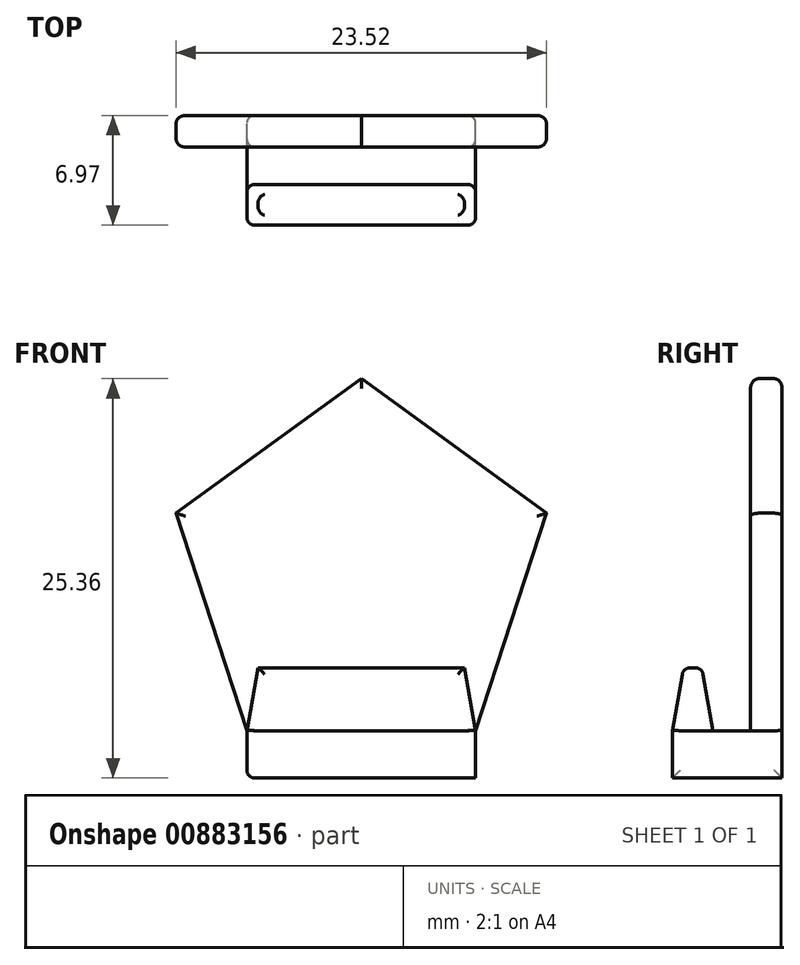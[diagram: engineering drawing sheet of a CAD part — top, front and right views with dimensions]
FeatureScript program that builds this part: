
annotation { "Feature Type Name" : "Feature", "Feature Type Description" : "" }
export const myFeature = defineFeature(function(context is Context, id is Id, definition is map)
    precondition{}
    {
        {
            var Q0;
            Q0=qCreatedBy(makeId("Front.planeOp"),FACE);
            var sketch = newSketch(context, id + "F0", { "sketchPlane" : qUnion([Q0])});
            skCircle(sketch, "E0.cCircle", {"center": v(0, 10) * mm, "radius": 10 * mm, "construction": true});
            skLineSegment(sketch, "E0.0", {"start": v(0, 22.36) * mm, "end": v(11.76, 13.82) * mm});
            skLineSegment(sketch, "E0.1", {"start": v(11.76, 13.82) * mm, "end": v(7.27, 0) * mm});
            skLineSegment(sketch, "E0.2", {"start": v(7.27, 0) * mm, "end": v(-7.27, 0) * mm});
            skLineSegment(sketch, "E0.3", {"start": v(-7.27, 0) * mm, "end": v(-11.76, 13.82) * mm});
            skLineSegment(sketch, "E0.4", {"start": v(-11.76, 13.82) * mm, "end": v(0, 22.36) * mm});
            skPoint(sketch, "E0.0.midPoint", {"position": v(5.88, 18.1) * mm});
            skSolve(sketch);
        }
        {
            var Q0;
            Q0=makeQuery(id+"F0.imprint","IMPRINT",FACE,{"disambiguationData":[TD([[makeQuery(id+"F0.imprint","IMPRINT",EDGE,{"derivedFrom":sQuery(id+"F0.wireOp",EDGE,"E0.0")}),-1.0]])]});
            extrude(context, id + "F1", {"entities" : qUnion([Q0]), "depth" : 2 * mm, "offsetDistance" : 25 * mm});
        }
        {
            var Q0;
            Q0=qCreatedBy(makeId("Top.planeOp"),FACE);
            var sketch = newSketch(context, id + "F2", { "sketchPlane" : qUnion([Q0])});
            skLineSegment(sketch, "E1.bottom", {"start": v(-7.27, -6.97) * mm, "end": v(7.27, -6.97) * mm});
            skLineSegment(sketch, "E1.top", {"start": v(-7.27, 0) * mm, "end": v(7.27, 0) * mm});
            skLineSegment(sketch, "E1.left", {"start": v(-7.27, -6.97) * mm, "end": v(-7.27, 0) * mm});
            skLineSegment(sketch, "E1.right", {"start": v(7.27, -6.97) * mm, "end": v(7.27, 0) * mm});
            skLineSegment(sketch, "E2", {"start": v(-7.27, -4.38) * mm, "end": v(7.27, -4.38) * mm});
            skSolve(sketch);
        }
        {
            var Q0;
            {var subQ0=sQuery(id+"F2.wireOp",EDGE,"E1.top");Q0=makeQuery(id+"F2.imprint","IMPRINT",FACE,{"disambiguationData":[TD([[makeQuery(id+"F2.imprint","IMPRINT",EDGE,{"derivedFrom":subQ0}),-1.0]])]});}
            var Q1;
            {var subQ0=sQuery(id+"F2.wireOp",EDGE,"E1.bottom");Q1=makeQuery(id+"F2.imprint","IMPRINT",FACE,{"disambiguationData":[TD([[makeQuery(id+"F2.imprint","IMPRINT",EDGE,{"derivedFrom":subQ0}),1.0]])]});}
            extrude(context, id + "F3", {"entities" : qUnion([Q0, Q1]), "operationType" : NewBodyOperationType.ADD, "oppositeDirection" : true, "depth" : 3 * mm, "offsetDistance" : 25 * mm});
        }
        {
            var Q0;
            {var subQ0=sQuery(id+"F2.wireOp",EDGE,"E1.bottom");Q0=makeQuery(id+"F2.imprint","IMPRINT",FACE,{"disambiguationData":[TD([[makeQuery(id+"F2.imprint","IMPRINT",EDGE,{"derivedFrom":subQ0}),1.0]])]});}
            extrude(context, id + "F4", {"entities" : qUnion([Q0]), "operationType" : NewBodyOperationType.ADD, "depth" : 4 * mm, "offsetDistance" : 25 * mm, "hasDraft" : true, "draftAngle" : 10 * degree, "draftPullDirection" : true});
        }
        {
            var Q0;
            Q0=makeQuery(id+"F4.opExtrude","SWEPT_EDGE",EDGE,{"disambiguationData":[OSD([sQuery(id+"F2.wireOp",EDGE,"E1.bottom"),sQuery(id+"F2.wireOp",EDGE,"E1.left")])]});
            var Q1;
            Q1=makeQuery(id+"F3.opExtrude","SWEPT_EDGE",EDGE,{"disambiguationData":[OSD([sQuery(id+"F2.wireOp",EDGE,"E1.bottom"),sQuery(id+"F2.wireOp",EDGE,"E1.left")])]});
            var Q2;
            Q2=makeQuery(id+"F4.opExtrude","CAP_EDGE",EDGE,{"disambiguationData":[OSD([sQuery(id+"F2.wireOp",EDGE,"E1.bottom")])],"isStart":false});
            var Q3;
            Q3=makeQuery(id+"F4.opExtrude","CAP_EDGE",EDGE,{"disambiguationData":[OSD([sQuery(id+"F2.wireOp",EDGE,"E2")])],"isStart":false});
            var Q4;
            Q4=makeQuery(id+"F3.opExtrude","CAP_EDGE",EDGE,{"disambiguationData":[OSD([sQuery(id+"F2.wireOp",EDGE,"E1.left")])],"isStart":false});
            var Q5;
            Q5=makeQuery(id+"F3.opExtrude","SWEPT_EDGE",EDGE,{"disambiguationData":[OSD([sQuery(id+"F2.wireOp",EDGE,"E1.bottom"),sQuery(id+"F2.wireOp",EDGE,"E1.right")])]});
            var Q6;
            Q6=makeQuery(id+"F4.opExtrude","SWEPT_EDGE",EDGE,{"disambiguationData":[OSD([sQuery(id+"F2.wireOp",EDGE,"E1.bottom"),sQuery(id+"F2.wireOp",EDGE,"E1.right")])]});
            var Q7;
            Q7=makeQuery(id+"F4.opExtrude","SWEPT_EDGE",EDGE,{"disambiguationData":[OSD([sQuery(id+"F2.wireOp",EDGE,"E1.right"),sQuery(id+"F2.wireOp",EDGE,"E2")])]});
            var Q8;
            Q8=makeQuery(id+"F4.opExtrude","SWEPT_EDGE",EDGE,{"disambiguationData":[OSD([sQuery(id+"F2.wireOp",EDGE,"E1.left"),sQuery(id+"F2.wireOp",EDGE,"E2")])]});
            var Q9;
            Q9=makeQuery(id+"F3.opExtrude","SWEPT_EDGE",EDGE,{"disambiguationData":[OSD([sQuery(id+"F2.wireOp",EDGE,"E1.top"),sQuery(id+"F2.wireOp",EDGE,"E1.left")])]});
            var Q10;
            Q10=makeQuery(id+"F1.opExtrude","CAP_EDGE",EDGE,{"disambiguationData":[OSD([sQuery(id+"F0.wireOp",EDGE,"E0.3")])],"isStart":true});
            var Q11;
            Q11=makeQuery(id+"F3.opExtrude","SWEPT_EDGE",EDGE,{"disambiguationData":[OSD([sQuery(id+"F2.wireOp",EDGE,"E1.top"),sQuery(id+"F2.wireOp",EDGE,"E1.right")])]});
            var Q12;
            Q12=makeQuery(id+"F1.opExtrude","CAP_EDGE",EDGE,{"disambiguationData":[OSD([sQuery(id+"F0.wireOp",EDGE,"E0.1")])],"isStart":true});
            var Q13;
            Q13=makeQuery(id+"F1.opExtrude","CAP_EDGE",EDGE,{"disambiguationData":[OSD([sQuery(id+"F0.wireOp",EDGE,"E0.0")])],"isStart":true});
            var Q14;
            Q14=makeQuery(id+"F1.opExtrude","CAP_EDGE",EDGE,{"disambiguationData":[OSD([sQuery(id+"F0.wireOp",EDGE,"E0.4")])],"isStart":true});
            var Q15;
            Q15=makeQuery(id+"F1.opExtrude","CAP_EDGE",EDGE,{"disambiguationData":[OSD([sQuery(id+"F0.wireOp",EDGE,"E0.0")])],"isStart":false});
            var Q16;
            Q16=makeQuery(id+"F1.opExtrude","CAP_EDGE",EDGE,{"disambiguationData":[OSD([sQuery(id+"F0.wireOp",EDGE,"E0.4")])],"isStart":false});
            var Q17;
            Q17=makeQuery(id+"F1.opExtrude","CAP_EDGE",EDGE,{"disambiguationData":[OSD([sQuery(id+"F0.wireOp",EDGE,"E0.3")])],"isStart":false});
            var Q18;
            Q18=makeQuery(id+"F1.opExtrude","CAP_EDGE",EDGE,{"disambiguationData":[OSD([sQuery(id+"F0.wireOp",EDGE,"E0.1")])],"isStart":false});
            fillet(context, id + "F5", {"entities" : qUnion([Q0, Q1, Q2, Q3, Q4, Q5, Q6, Q7, Q8, Q9, Q10, Q11, Q12, Q13, Q14, Q15, Q16, Q17, Q18]), "radius" : 0.5 * mm, "tangentPropagation" : true, "allowEdgeOverflow" : false});
        }
    });
